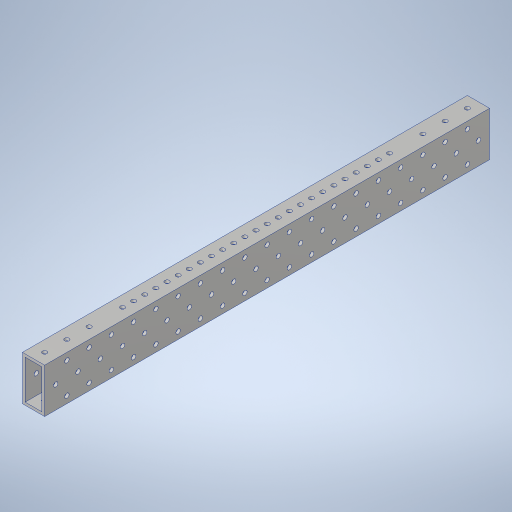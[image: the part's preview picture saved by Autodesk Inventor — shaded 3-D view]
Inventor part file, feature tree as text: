
AUTODESK INVENTOR PART (.ipt)
format: ipt  version: 2023.4 (Build 274418000, 418)  size: 440,832 bytes
history: native  units: in
note: dims shown in document units (in); Inventor stores cm internally (conversion verified against a paired STEP export)
features: hole x2, sketch x2, extrude x1, projected_geometry x1
ambient origin geometry x8: Origin, YZ Plane, XZ Plane, XY Plane, X Axis, Y Axis, Z Axis, Center Point
bodies: Solid1 (feature_tree)
feature tree (6):
  extrude  "Extrusion1"  Depth=0.5in
  hole  "Hole1"  [1 undecoded]
  hole  "Hole2"  [1 undecoded]
  sketch  "Sketch2"  dims[d4=0.0in d5=0.5in]
  sketch  "Sketch3"  dims[d6=1.0in d7=1.0in d8=1.0in d9=4.7244in d11=0.5in d12=0.3937in d14=1.0in d16=4.7244in d18=0.5in d19=0.3937in d21=1.0in d23=0.201in d24=0.75in d25=0.385in d26=0.25in d27=0.5635in d28=0.0055in d29=0.8108in d31=0.5in d33=0.375in d34=0.375in d35=0.5in d36=3.937in d38=1.0in d39=0.3937in d41=1.0in d43=3.937in d45=1.0in d46=0.3937in d48=1.0in d50=0.201in d51=0.75in d52=0.375in d53=0.25in d54=0.5635in d55=1.0in d56=0.8108in]
  projected_geometry  "Projected Loop1"
note: 2 required parameter values undecoded (feature->parameter linkage not recoverable at this tier; creation-order binding heuristic only, values carry confidence <= 0.55)
